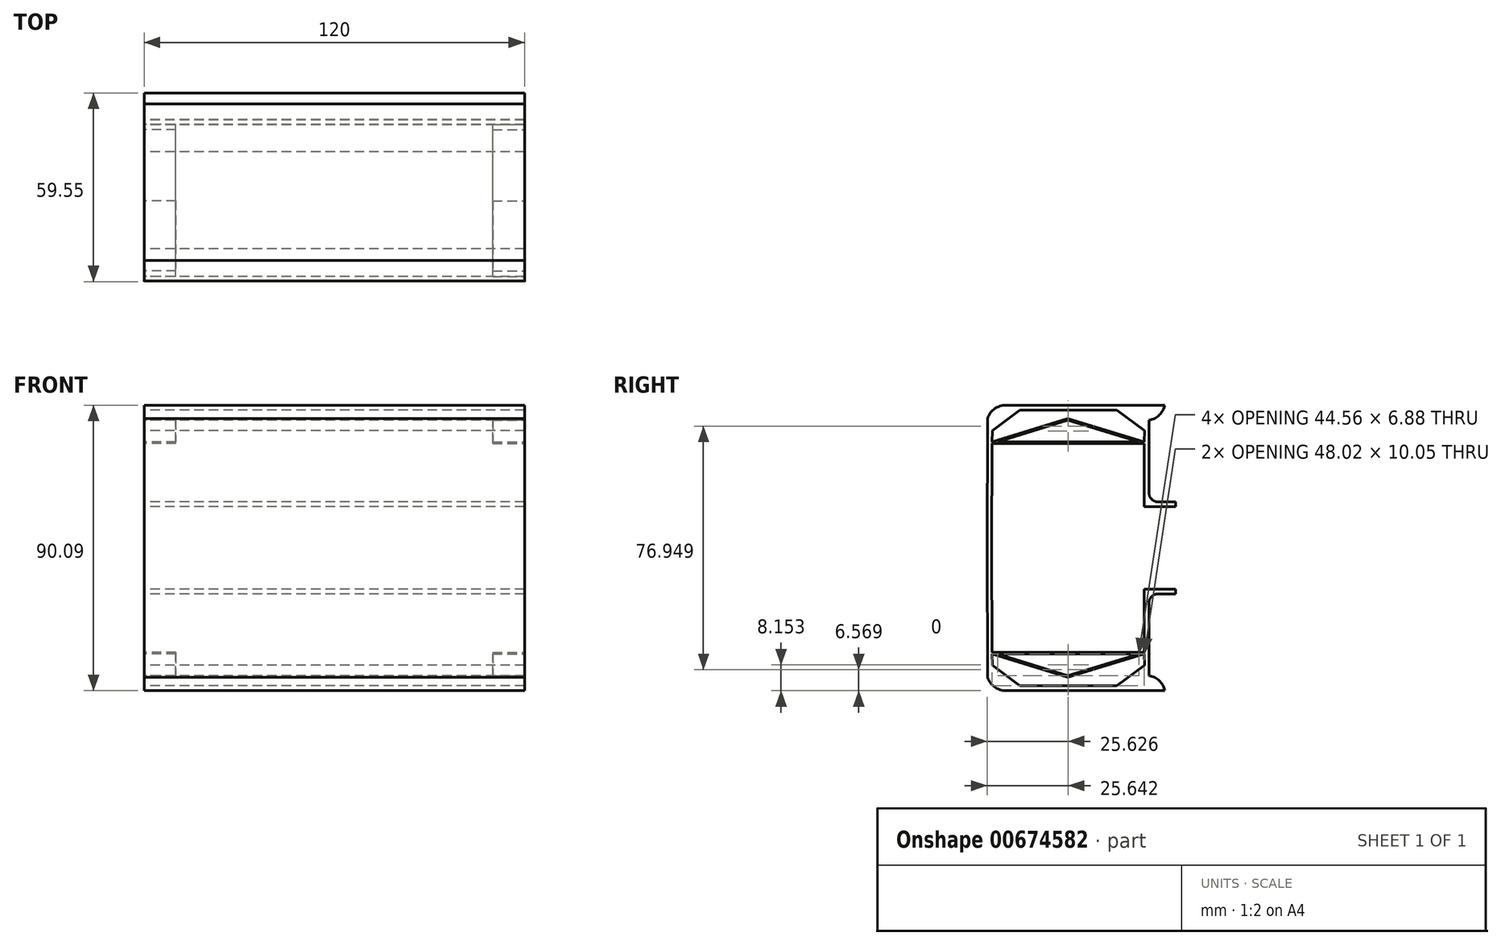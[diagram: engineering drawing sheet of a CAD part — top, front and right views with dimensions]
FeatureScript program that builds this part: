
annotation { "Feature Type Name" : "Feature", "Feature Type Description" : "" }
export const myFeature = defineFeature(function(context is Context, id is Id, definition is map)
    precondition{}
    {
        {
            var Q0;
            Q0=qCreatedBy(makeId("Right.planeOp"),FACE);
            var sketch = newSketch(context, id + "F0", { "sketchPlane" : qUnion([Q0])});
            skLineSegment(sketch, "E0.top", {"start": v(15.43, -49.8) * mm, "end": v(-15.15, -49.8) * mm});
            skLineSegment(sketch, "E0.right", {"start": v(-24.01, -6.3) * mm, "end": v(-23.86, -43.26) * mm});
            skPoint(sketch, "E0.middle", {"position": v(0, 0) * mm});
            skPoint(sketch, "E1", {"position": v(24.04, -19.3) * mm});
            skLineSegment(sketch, "E2.trimOffspring", {"start": v(24.04, -19.3) * mm, "end": v(24.14, -43.26) * mm});
            skPoint(sketch, "E3.visualSharp", {"position": v(-23.83, -49.8) * mm});
            skPoint(sketch, "E4.visualSharp", {"position": v(24.17, -49.8) * mm});
            skLineSegment(sketch, "E5", {"start": v(24.04, -19.3) * mm, "end": v(34.04, -19.3) * mm});
            skLineSegment(sketch, "E6.0", {"start": v(28.56, -20.8) * mm, "end": v(34.04, -20.8) * mm});
            skLineSegment(sketch, "E6.6", {"start": v(-25.51, -6.3) * mm, "end": v(-25.35, -47.07) * mm});
            skArc(sketch, "E6.7", {"start": v(-25.35, -47.07) * mm, "mid": v(-22.86, -50.37) * mm, "end": v(-18.83, -51.3) * mm});
            skLineSegment(sketch, "E6.8", {"start": v(30.57, -51.3) * mm, "end": v(-18.83, -51.3) * mm});
            skArc(sketch, "E6.9", {"start": v(30.57, -51.3) * mm, "mid": v(28.84, -48.2) * mm, "end": v(25.65, -46.63) * mm});
            skLineSegment(sketch, "E6.10", {"start": v(25.56, -23.8) * mm, "end": v(25.65, -46.63) * mm});
            skLineSegment(sketch, "E7", {"start": v(34.04, -19.3) * mm, "end": v(34.04, -20.8) * mm});
            skPoint(sketch, "E8.visualSharp", {"position": v(25.55, -20.8) * mm});
            skArc(sketch, "E8.filletArc", {"start": v(28.56, -20.8) * mm, "mid": v(26.43, -21.68) * mm, "end": v(25.56, -23.8) * mm});
            skLineSegment(sketch, "E9", {"start": v(-24.01, -6.3) * mm, "end": v(-25.51, -6.3) * mm});
            skLineSegment(sketch, "E10", {"start": v(-25.51, -6.3) * mm, "end": v(43.63, -6.3) * mm, "construction": true});
            skLineSegment(sketch, "E11", {"start": v(-23.86, -43.26) * mm, "end": v(-15.15, -49.8) * mm});
            skLineSegment(sketch, "E12", {"start": v(24.14, -43.26) * mm, "end": v(15.43, -49.8) * mm});
            skSolve(sketch);
        }
        {
            var Q0;
            Q0 = qSketchRegion(id + "F0", true);
            extrude(context, id + "F1", {"entities" : qUnion([Q0]), "depth" : 60 * mm, "offsetDistance" : 25 * mm});
        }
        {
            var Q0;
            Q0=makeQuery(id+"F1.opExtrude","CAP_FACE",FACE,{"disambiguationData":[OSD([sQuery(id+"F0.wireOp",EDGE,"E0.bottom"),sQuery(id+"F0.wireOp",EDGE,"E0.top"),sQuery(id+"F0.wireOp",EDGE,"E0.left"),sQuery(id+"F0.wireOp",EDGE,"E0.right"),sQuery(id+"F0.wireOp",EDGE,"E2.trimOffspring"),sQuery(id+"F0.wireOp",EDGE,"16ec7434-7e19-4c96-ad34-d09fe3e63414.filletArc"),sQuery(id+"F0.wireOp",EDGE,"782e88cc-4596-4778-937f-94acf3693ae4.filletArc"),sQuery(id+"F0.wireOp",EDGE,"E3.filletArc"),sQuery(id+"F0.wireOp",EDGE,"E4.filletArc"),sQuery(id+"F0.wireOp",EDGE,"0f476a3a-29cd-4e09-8ddb-883452e4d05f"),sQuery(id+"F0.wireOp",EDGE,"E5"),sQuery(id+"F0.wireOp",EDGE,"E6.0"),sQuery(id+"F0.wireOp",EDGE,"E6.1"),sQuery(id+"F0.wireOp",EDGE,"E6.2"),sQuery(id+"F0.wireOp",EDGE,"E6.3"),sQuery(id+"F0.wireOp",EDGE,"E6.4"),sQuery(id+"F0.wireOp",EDGE,"E6.5"),sQuery(id+"F0.wireOp",EDGE,"E6.6"),sQuery(id+"F0.wireOp",EDGE,"E6.7"),sQuery(id+"F0.wireOp",EDGE,"E6.8"),sQuery(id+"F0.wireOp",EDGE,"E6.9"),sQuery(id+"F0.wireOp",EDGE,"E6.10"),sQuery(id+"F0.wireOp",EDGE,"E7"),sQuery(id+"F0.wireOp",EDGE,"56edb3b3-d3ca-4cde-a283-c5cd5add8c42"),sQuery(id+"F0.wireOp",EDGE,"E8.filletArc"),sQuery(id+"F0.wireOp",EDGE,"69a5be2d-b862-4d8c-9c8a-7a6ed0181d43.filletArc")])],"isStart":false});
            var sketch = newSketch(context, id + "F2", { "sketchPlane" : qUnion([Q0])});
            skLineSegment(sketch, "E13", {"start": v(-23.88, -39.24) * mm, "end": v(24.12, -39.24) * mm});
            skLineSegment(sketch, "E14", {"start": v(-22.17, -39.75) * mm, "end": v(22.4, -39.75) * mm});
            skLineSegment(sketch, "E15", {"start": v(-23.88, -39.75) * mm, "end": v(3.49, -48.24) * mm});
            skLineSegment(sketch, "E16", {"start": v(-8.58, -49.8) * mm, "end": v(8.49, -49.8) * mm});
            skLineSegment(sketch, "E17", {"start": v(-3.58, -48.26) * mm, "end": v(24.12, -39.75) * mm});
            skLineSegment(sketch, "E18", {"start": v(0, -46.63) * mm, "end": v(22.4, -39.75) * mm});
            skLineSegment(sketch, "E19", {"start": v(0, -46.63) * mm, "end": v(-22.17, -39.75) * mm});
            skLineSegment(sketch, "E20", {"start": v(-22.17, -39.75) * mm, "end": v(-22.32, -40.23) * mm, "construction": true});
            skLineSegment(sketch, "E21", {"start": v(22.4, -39.75) * mm, "end": v(22.55, -40.23) * mm, "construction": true});
            skLineSegment(sketch, "E22", {"start": v(0.12, -39.24) * mm, "end": v(0.12, -39.75) * mm, "construction": true});
            skLineSegment(sketch, "E23", {"start": v(-3.58, -48.26) * mm, "end": v(-3.58, -49.8) * mm});
            skLineSegment(sketch, "E24", {"start": v(3.49, -48.24) * mm, "end": v(3.49, -49.8) * mm});
            skSolve(sketch);
        }
        {
            var Q0;
            {var subQ1=sQuery(id+"F2.wireOp",EDGE,"E13");Q0=makeQuery(id+"F2.imprint","IMPRINT",FACE,{"disambiguationData":[TD([[makeQuery(id+"F2.imprint","IMPRINT",EDGE,{"derivedFrom":subQ1}),-1.0]])]});}
            var Q1;
            {var subQ0=sQuery(id+"F2.wireOp",EDGE,"69ec383f-f7ca-4513-a4e7-9af87f1944310.MirrorCS");Q1=makeQuery(id+"F2.imprint","IMPRINT",FACE,{"disambiguationData":[TD([[makeQuery(id+"F2.imprint","IMPRINT",EDGE,{"derivedFrom":subQ0}),-1.0]])]});}
            extrude(context, id + "F3", {"entities" : qUnion([Q0, Q1]), "operationType" : NewBodyOperationType.ADD, "oppositeDirection" : true, "depth" : 10 * mm, "offsetDistance" : 25 * mm});
        }
        {
            var Q0;
            Q0=makeQuery(id+"F1.opExtrude","SWEPT_BODY",BODY,{"disambiguationData":[OSD([sQuery(id+"F0.wireOp",EDGE,"E0.bottom"),sQuery(id+"F0.wireOp",EDGE,"E0.top"),sQuery(id+"F0.wireOp",EDGE,"E0.left"),sQuery(id+"F0.wireOp",EDGE,"E0.right"),sQuery(id+"F0.wireOp",EDGE,"E2.trimOffspring"),sQuery(id+"F0.wireOp",EDGE,"16ec7434-7e19-4c96-ad34-d09fe3e63414.filletArc"),sQuery(id+"F0.wireOp",EDGE,"782e88cc-4596-4778-937f-94acf3693ae4.filletArc"),sQuery(id+"F0.wireOp",EDGE,"E3.filletArc"),sQuery(id+"F0.wireOp",EDGE,"E4.filletArc"),sQuery(id+"F0.wireOp",EDGE,"0f476a3a-29cd-4e09-8ddb-883452e4d05f"),sQuery(id+"F0.wireOp",EDGE,"E5"),sQuery(id+"F0.wireOp",EDGE,"E6.0"),sQuery(id+"F0.wireOp",EDGE,"E6.1"),sQuery(id+"F0.wireOp",EDGE,"E6.2"),sQuery(id+"F0.wireOp",EDGE,"E6.3"),sQuery(id+"F0.wireOp",EDGE,"E6.4"),sQuery(id+"F0.wireOp",EDGE,"E6.5"),sQuery(id+"F0.wireOp",EDGE,"E6.6"),sQuery(id+"F0.wireOp",EDGE,"E6.7"),sQuery(id+"F0.wireOp",EDGE,"E6.8"),sQuery(id+"F0.wireOp",EDGE,"E6.9"),sQuery(id+"F0.wireOp",EDGE,"E6.10"),sQuery(id+"F0.wireOp",EDGE,"E7"),sQuery(id+"F0.wireOp",EDGE,"56edb3b3-d3ca-4cde-a283-c5cd5add8c42"),sQuery(id+"F0.wireOp",EDGE,"E8.filletArc"),sQuery(id+"F0.wireOp",EDGE,"69a5be2d-b862-4d8c-9c8a-7a6ed0181d43.filletArc")])]});
            var Q1;
            Q1=qCreatedBy(makeId("Right.planeOp"),FACE);
            mirror(context, id + "F4", {"operationType" : NewBodyOperationType.ADD, "entities" : qUnion([Q0]), "mirrorPlane" : qUnion([Q1])});
        }
        {
            var Q0;
            Q0=makeQuery(id+"F1.opExtrude","SWEPT_BODY",BODY,{"disambiguationData":[OSD([sQuery(id+"F0.wireOp",EDGE,"E0.top"),sQuery(id+"F0.wireOp",EDGE,"E0.right"),sQuery(id+"F0.wireOp",EDGE,"E2.trimOffspring"),sQuery(id+"F0.wireOp",EDGE,"E3.filletArc"),sQuery(id+"F0.wireOp",EDGE,"E4.filletArc"),sQuery(id+"F0.wireOp",EDGE,"E5"),sQuery(id+"F0.wireOp",EDGE,"E6.0"),sQuery(id+"F0.wireOp",EDGE,"E6.6"),sQuery(id+"F0.wireOp",EDGE,"E6.7"),sQuery(id+"F0.wireOp",EDGE,"E6.8"),sQuery(id+"F0.wireOp",EDGE,"E6.9"),sQuery(id+"F0.wireOp",EDGE,"E6.10"),sQuery(id+"F0.wireOp",EDGE,"E7"),sQuery(id+"F0.wireOp",EDGE,"E8.filletArc"),sQuery(id+"F0.wireOp",EDGE,"E9")])]});
            var Q1;
            {var subQ0=makeQuery(id+"F1.opExtrude","SWEPT_FACE",FACE,{"disambiguationData":[OSD([sQuery(id+"F0.wireOp",EDGE,"E9")])]});Q1=makeQuery(id+"F4.boolean.opBoolean","MERGE",FACE,{"derivedFrom":[subQ0,makeQuery(id+"F4.opPattern","COPY",FACE,{"derivedFrom":subQ0,"instanceName":"1"})]});}
            mirror(context, id + "F5", {"operationType" : NewBodyOperationType.ADD, "entities" : qUnion([Q0]), "mirrorPlane" : qUnion([Q1])});
        }
    });
